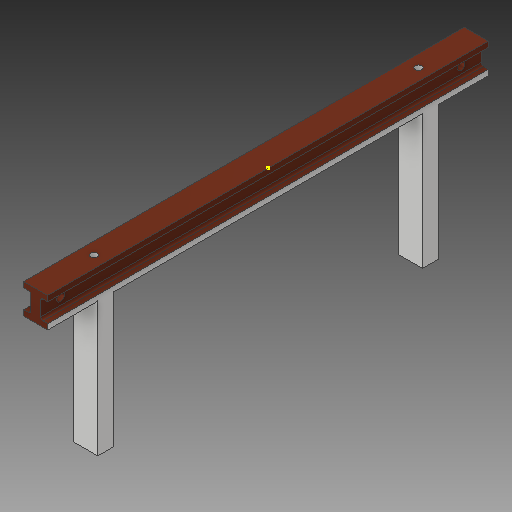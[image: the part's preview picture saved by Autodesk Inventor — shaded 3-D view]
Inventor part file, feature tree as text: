
AUTODESK INVENTOR PART (.ipt)
format: ipt  version: 2019 (Build 230136000, 136)  size: 185,856 bytes
history: native  units: mm
features: sketch x5, hole x4, extrude x2
ambient origin geometry x8: Origin, YZ Plane, XZ Plane, XY Plane, X Axis, Y Axis, Z Axis, Center Point
bodies: Solid1 (feature_tree)
feature tree (11):
  extrude  "Extrusion1"  Depth=38.0mm
  hole  "Hole1"  [1 undecoded]
  hole  "Hole2"  [1 undecoded]
  extrude  "Extrusion2"  Depth=7.0mm
  sketch  "Sketch5"  dims[d4=9.0mm d6=7.0mm]
  hole  "Hole5"  [1 undecoded]
  hole  "Hole6"  [1 undecoded]
  sketch  "Sketch1"  dims[d0=30.5mm d1=38.0mm]
  sketch  "Sketch2"  dims[d2=7.0mm d3=7.0mm]
  sketch  "Sketch8"  dims[d7=9.0mm d8=7.0mm]
  sketch  "Sketch9"  dims[d9=3.0mm d11=3.0mm d12=558.8mm d13=0.0mm d14=25.4mm d24=9.0mm d16=10.0mm d17=6.0mm d18=4.0mm d19=2.0mm d20=90.0deg d21=25.0mm d22=0.0mm d23=25.4mm d25=9.0mm d26=10.0mm d27=6.0mm d28=4.0mm d29=2.0mm d30=90.0deg d31=25.0mm d32=20.594885mm d33=63.5mm d34=20.0mm d35=30.5mm d36=63.5mm d37=20.0mm d38=170.0mm d39=0.0mm d72=15.0mm d73=10.0mm d74=8.647mm d75=20.0mm d76=4.0mm d77=2.0mm d78=90.0deg d79=8.0mm d80=20.594885mm d81=15.0mm d82=10.0mm d83=8.647mm d84=20.0mm d85=4.0mm d86=2.0mm d87=90.0deg d88=8.0mm d89=20.594885mm]
note: 4 required parameter values undecoded (feature->parameter linkage not recoverable at this tier; creation-order binding heuristic only, values carry confidence <= 0.55)
